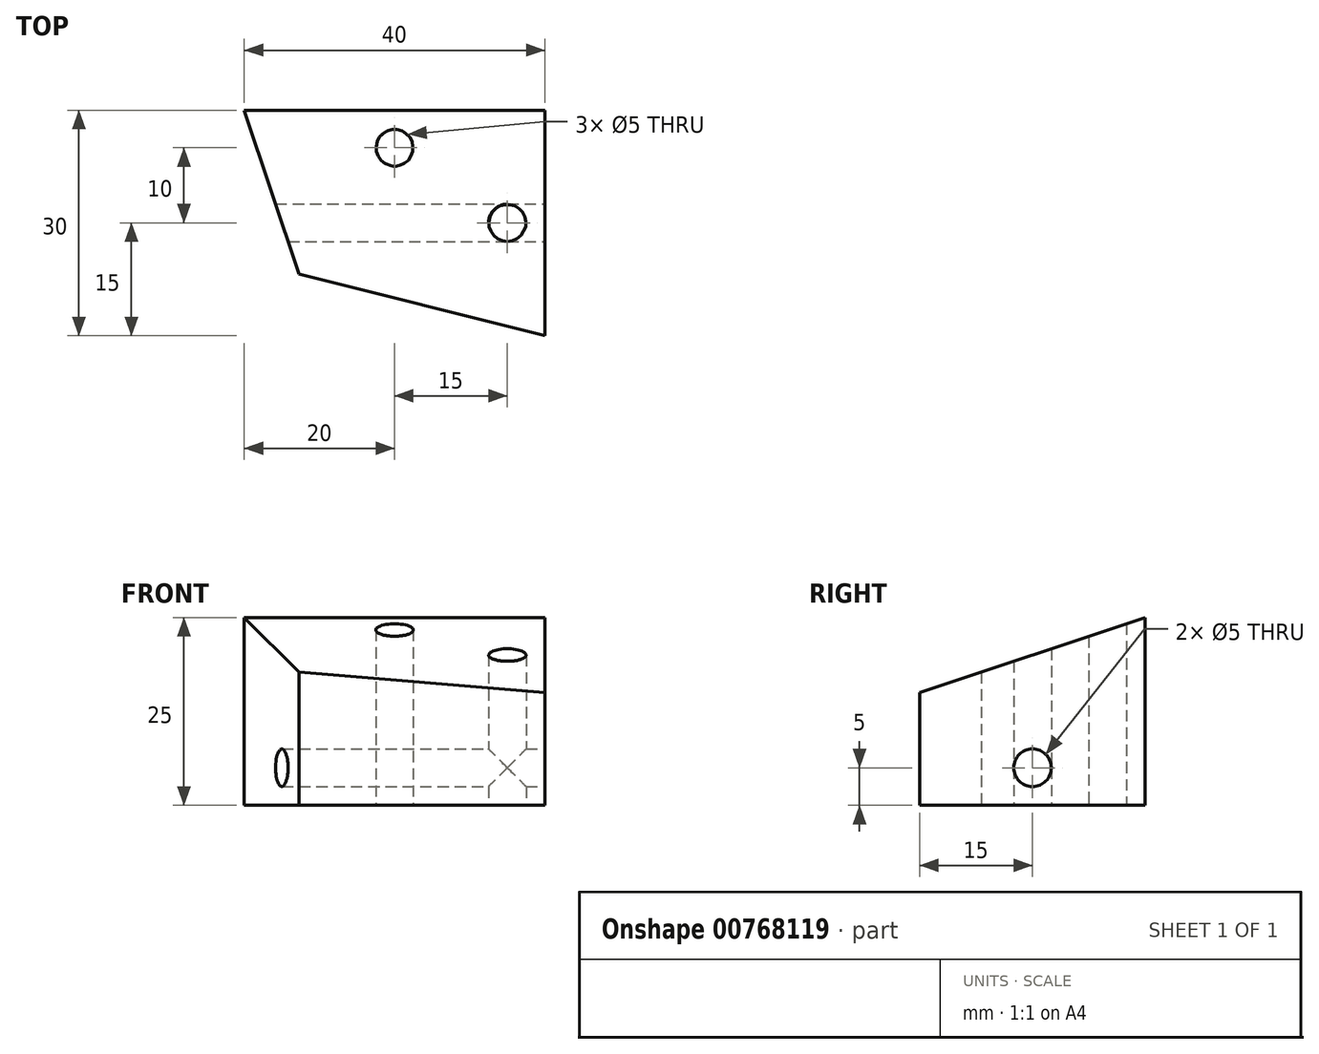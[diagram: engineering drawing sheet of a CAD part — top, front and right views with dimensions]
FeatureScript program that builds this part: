
annotation { "Feature Type Name" : "Feature", "Feature Type Description" : "" }
export const myFeature = defineFeature(function(context is Context, id is Id, definition is map)
    precondition{}
    {
        {
            var Q0;
            Q0=qCreatedBy(makeId("Top.planeOp"),FACE);
            var sketch = newSketch(context, id + "F0", { "sketchPlane" : qUnion([Q0])});
            skLineSegment(sketch, "E0.bottom", {"start": v(20, 15) * mm, "end": v(-20, 15) * mm});
            skLineSegment(sketch, "E0.top", {"start": v(20, -15) * mm, "end": v(-20, -15) * mm});
            skLineSegment(sketch, "E0.left", {"start": v(20, 15) * mm, "end": v(20, -15) * mm});
            skLineSegment(sketch, "E0.right", {"start": v(-20, 15) * mm, "end": v(-20, -15) * mm});
            skPoint(sketch, "E0.middle", {"position": v(0, 0) * mm});
            skLineSegment(sketch, "E1", {"start": v(-20, 15) * mm, "end": v(-10, -15) * mm});
            skLineSegment(sketch, "E2", {"start": v(20, -15) * mm, "end": v(-20, -5) * mm});
            skPoint(sketch, "E3.orphan", {"position": v(20, -5) * mm});
            skCircle(sketch, "E4", {"center": v(15, 0) * mm, "radius": 2.5 * mm});
            skCircle(sketch, "E5", {"center": v(0, 10) * mm, "radius": 2.5 * mm});
            skSolve(sketch);
        }
        {
            var Q0;
            {var subQ1=sQuery(id+"F0.wireOp",EDGE,"E0.bottom");Q0=makeQuery(id+"F0.imprint","IMPRINT",FACE,{"disambiguationData":[TD([[makeQuery(id+"F0.imprint","IMPRINT",EDGE,{"derivedFrom":subQ1}),1.0]])]});}
            extrude(context, id + "F1", {"entities" : qUnion([Q0]), "depth" : 25 * mm, "offsetDistance" : 25 * mm});
        }
        {
            var Q0;
            Q0=makeQuery(id+"F1.opExtrude","SWEPT_FACE",FACE,{"disambiguationData":[OSD([sQuery(id+"F0.wireOp",EDGE,"E0.left")])]});
            var sketch = newSketch(context, id + "F2", { "sketchPlane" : qUnion([Q0])});
            skLineSegment(sketch, "E6", {"start": v(15, 25) * mm, "end": v(-15, 15) * mm});
            skLineSegment(sketch, "E7.1", {"start": v(15, 25) * mm, "end": v(-15, 25) * mm});
            skLineSegment(sketch, "E7.2", {"start": v(-15, 25) * mm, "end": v(-15, 0) * mm});
            skCircle(sketch, "E8", {"center": v(0, 5) * mm, "radius": 2.5 * mm});
            skSolve(sketch);
        }
        {
            var Q0;
            Q0=makeQuery(id+"F2.imprint","IMPRINT",FACE,{"disambiguationData":[TD([[makeQuery(id+"F2.imprint","IMPRINT",EDGE,{"derivedFrom":sQuery(id+"F2.wireOp",EDGE,"E8")}),1.0]])]});
            var Q1;
            {var subQ0=sQuery(id+"F2.wireOp",EDGE,"E6");Q1=makeQuery(id+"F2.imprint","IMPRINT",FACE,{"disambiguationData":[TD([[makeQuery(id+"F2.imprint","IMPRINT",EDGE,{"derivedFrom":subQ0}),-1.0]])]});}
            var Q2;
            Q2=sQuery(id+"F2.wireOp",EDGE,"E8");
            extrude(context, id + "F3", {"entities" : qUnion([Q0, Q1]), "operationType" : NewBodyOperationType.REMOVE, "surfaceEntities" : qUnion([Q2]), "endBound" : BoundingType.THROUGH_ALL, "oppositeDirection" : true, "depth" : 25 * mm, "offsetDistance" : 25 * mm});
        }
    });
